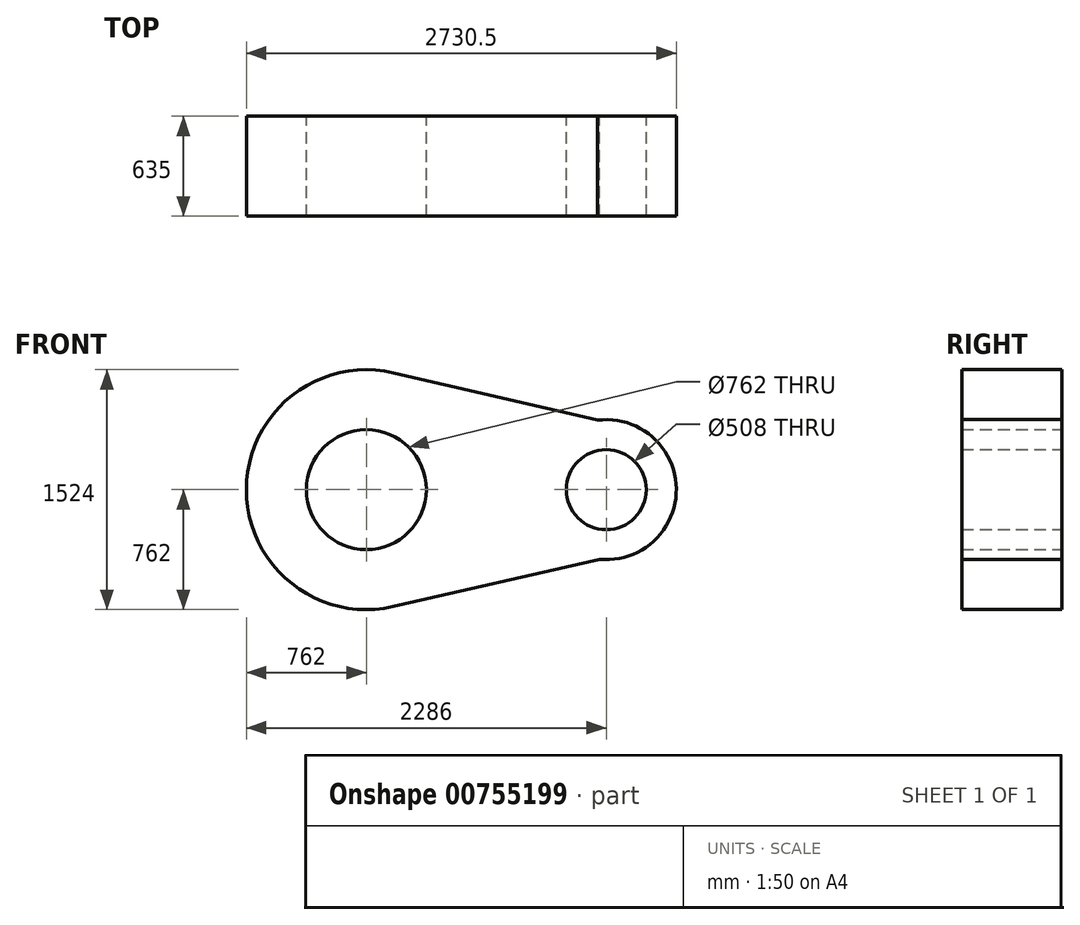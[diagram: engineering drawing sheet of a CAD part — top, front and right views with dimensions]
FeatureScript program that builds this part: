
annotation { "Feature Type Name" : "Feature", "Feature Type Description" : "" }
export const myFeature = defineFeature(function(context is Context, id is Id, definition is map)
    precondition{}
    {
        {
            var Q0;
            Q0=qCreatedBy(makeId("Front.planeOp"),FACE);
            var sketch = newSketch(context, id + "F0", { "sketchPlane" : qUnion([Q0])});
            skCircle(sketch, "E0", {"center": v(0, 0) * mm, "radius": 762 * mm});
            skCircle(sketch, "E1", {"center": v(1524, 0) * mm, "radius": 444.5 * mm});
            skCircle(sketch, "E2", {"center": v(0, 0) * mm, "radius": 381 * mm});
            skCircle(sketch, "E3", {"center": v(1524, 0) * mm, "radius": 254 * mm});
            skLineSegment(sketch, "E4", {"start": v(172.43, 742.24) * mm, "end": v(1468.86, 441.07) * mm});
            skLineSegment(sketch, "E5", {"start": v(170.13, -742.76) * mm, "end": v(1481.28, -442.44) * mm});
            skSolve(sketch);
        }
        {
            var Q0;
            Q0 = qSketchRegion(id + "F0", true);
            extrude(context, id + "F1", {"entities" : qUnion([Q0]), "depth" : 635 * mm, "offsetDistance" : 25.4 * mm});
        }
    });
